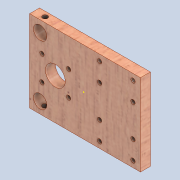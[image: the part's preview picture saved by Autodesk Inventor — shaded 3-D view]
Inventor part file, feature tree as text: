
AUTODESK INVENTOR PART (.ipt)
format: ipt  version: 2020 (Build 240168000, 168)  size: 297,472 bytes
history: native  units: mm
features: sketch x7, other x6, extrude x4, hole x3, pattern_linear x2, reference x2, direct_edit x1, move_body x1
ambient origin geometry x8: Origin, YZ Plane, XZ Plane, XY Plane, X Axis, Y Axis, Z Axis, Center Point
bodies: Solid1 (feature_tree)
feature tree (26):
  extrude  "Extrusion1"  Depth=66.0mm
  extrude  "Extrusion4"  TaperAngle=0.0deg  [1 undecoded]
  extrude  "Extrusion5"  TaperAngle=0.0deg  [1 undecoded]
  extrude  "Extrusion6"  Depth=9.0mm
  sketch  "Sketch7"  dims[d27=8.5mm d28=9.0mm]
  hole  "Hole1"  [1 undecoded]
  direct_edit  "Direct Edit1"
  pattern_linear  "Rectangular Pattern2"  Spacing1=3.5mm  [1 undecoded]
  pattern_linear  "Rectangular Pattern3"  Spacing1=21.5mm  [1 undecoded]
  hole  "Hole2"  [1 undecoded]
  hole  "Hole3"  [1 undecoded]
  sketch  "Sketch1"  dims[d0=87.5mm d1=66.0mm]
  sketch  "Sketch4"  dims[d2=8.0mm d3=0.0mm d19=0.0mm d20=0.0mm]
  sketch  "Sketch6"  dims[d24=16.0mm d25=0.0mm d26=0.0mm]
  sketch  "Sketch8"  dims[d29=10.8mm d30=9.0mm]
  reference  "Reference7"
  reference  "Reference8"
  sketch  "Sketch10"  dims[d31=0.0mm d32=0.0mm]
  sketch  "Sketch11"  dims[d33=20.748842mm d35=3.5mm d36=21.5mm d37=20.0mm d38=4.0mm d39=5.0mm d40=15.0mm d41=5.0mm d42=15.0mm d43=3.5mm d44=6.0mm d45=4.0mm d46=2.0mm d47=90.0deg d48=8.0mm d49=20.594885mm d53=0.0mm d54=0.0mm d55=2.0mm d56=26.0mm d57=20.0mm d59=15.0mm d60=20.0mm d62=41.0mm d63=20.0mm d65=27.0mm d66=8.5mm d67=4.134mm d68=5.0mm d69=4.0mm d70=2.0mm d71=90.0deg d72=7.45mm d73=20.594885mm d74=8.5mm d75=4.134mm d76=5.0mm d77=4.0mm d78=2.0mm d79=90.0deg d80=7.45mm d81=20.594885mm]
  parser-record x1  (decoder bookkeeping rows leaked as tree rows — omitted from the tree; the rows remain in map.json)
  other  "0005-00-00 Ansamblu_General.iam"
  other  "Surub M4 saiba piulita.iam:65"
  other  "0005-10-1013 ISO 7089 - 4 - 140 HV.ipt:2"
  move_body  "Move1"
  other  "0005-10-04 Z axis and extruder.iam"
  other  "0005-10-1002  Hub.ipt:22"
note: 7 required parameter values undecoded (feature->parameter linkage not recoverable at this tier; creation-order binding heuristic only, values carry confidence <= 0.55)
note: 1 file-system path scrubbed to <path> (originals preserved in map.json)
